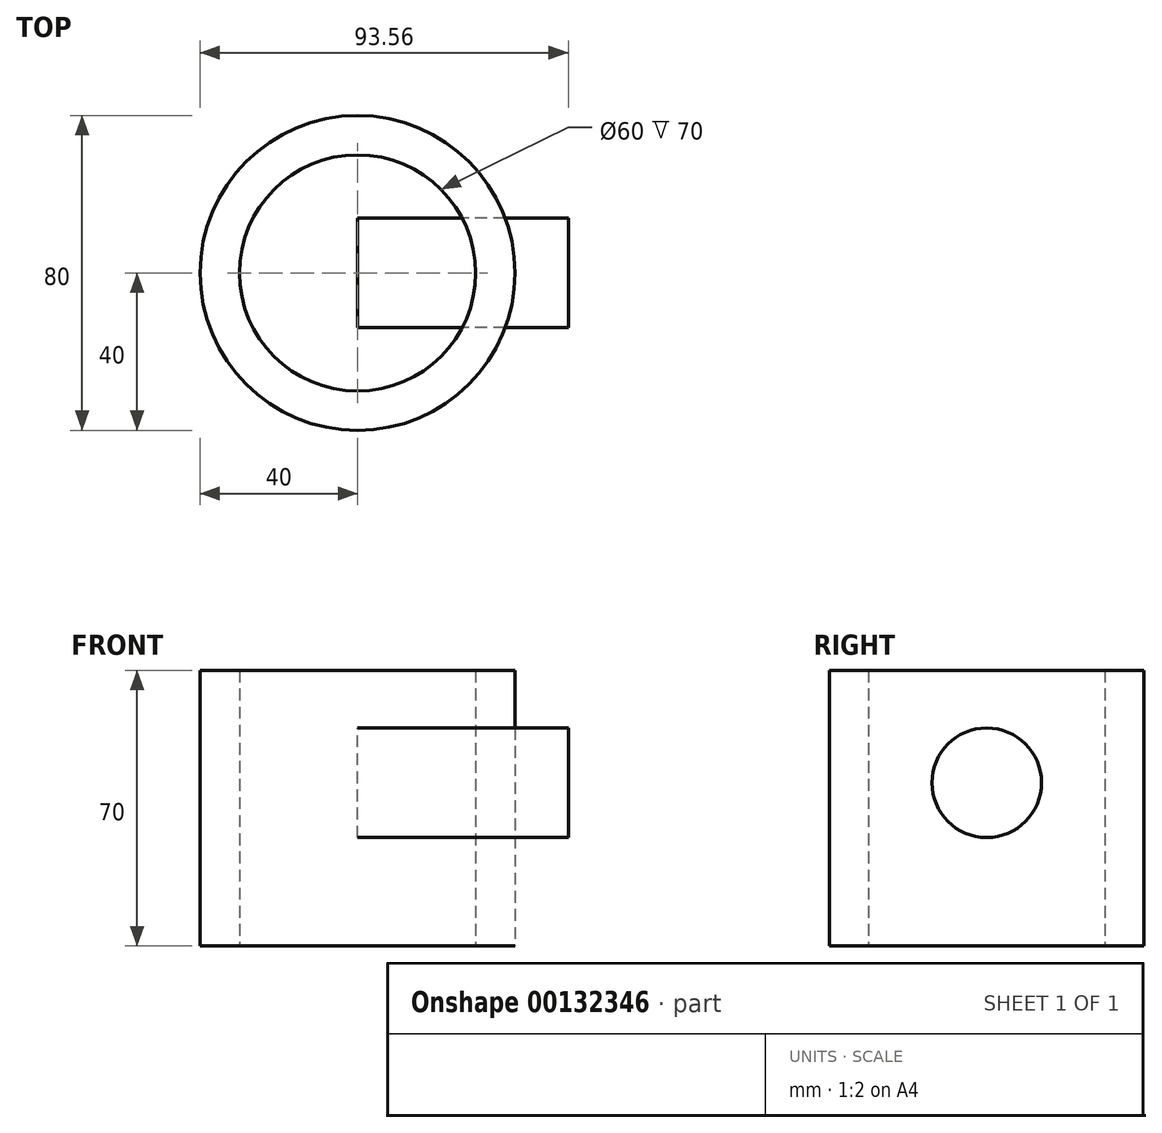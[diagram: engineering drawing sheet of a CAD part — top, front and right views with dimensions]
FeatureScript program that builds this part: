
annotation { "Feature Type Name" : "Feature", "Feature Type Description" : "" }
export const myFeature = defineFeature(function(context is Context, id is Id, definition is map)
    precondition{}
    {
        {
            var Q0;
            Q0=qCreatedBy(makeId("Top.planeOp"),FACE);
            var sketch = newSketch(context, id + "F0", { "sketchPlane" : qUnion([Q0])});
            skCircle(sketch, "E0", {"center": v(0, 0) * mm, "radius": 40 * mm});
            skCircle(sketch, "E1", {"center": v(0, 0) * mm, "radius": 30 * mm});
            skSolve(sketch);
        }
        {
            var Q0;
            Q0 = qSketchRegion(id + "F0", true);
            extrude(context, id + "F1", {"entities" : qUnion([Q0]), "depth" : 70 * mm});
        }
        {
            var Q0;
            Q0=qCreatedBy(makeId("Right.planeOp"),FACE);
            var sketch = newSketch(context, id + "F2", { "sketchPlane" : qUnion([Q0])});
            skCircle(sketch, "E2", {"center": v(0, 41.47) * mm, "radius": 13.92 * mm});
            skSolve(sketch);
        }
        {
            var Q0;
            Q0 = qSketchRegion(id + "F2", true);
            extrude(context, id + "F3", {"entities" : qUnion([Q0]), "depth" : 53.56 * mm});
        }
    });
